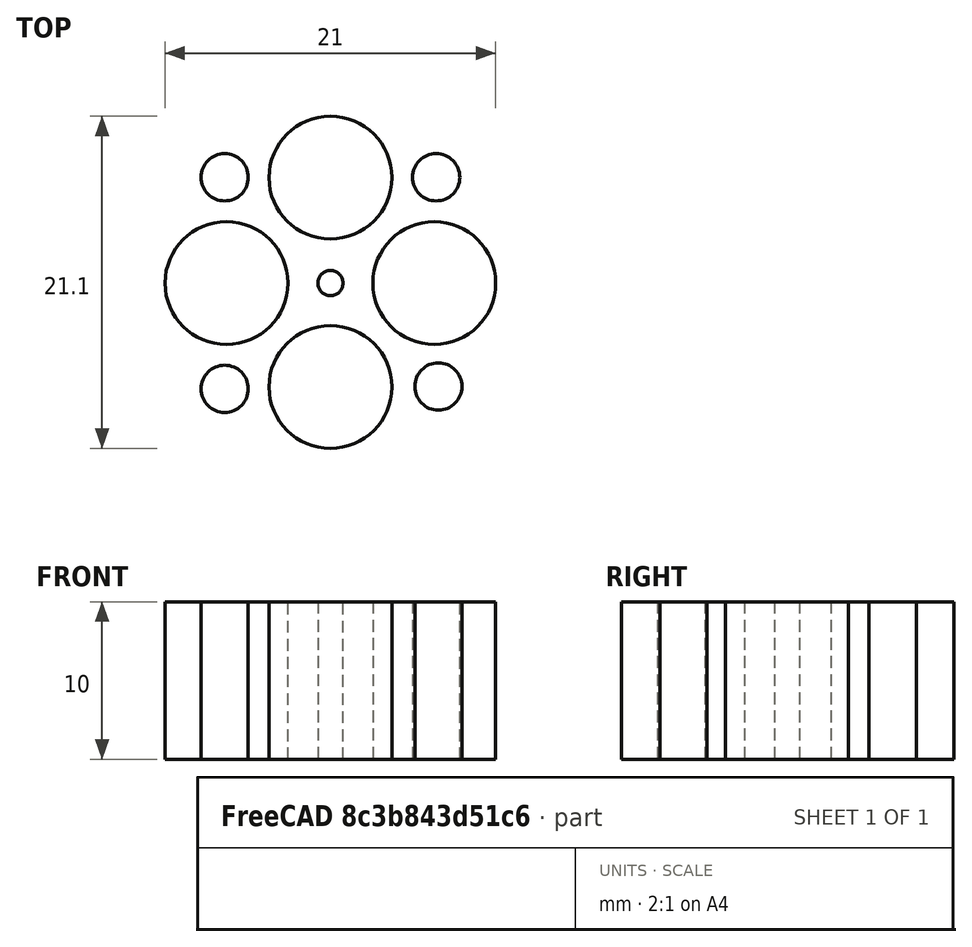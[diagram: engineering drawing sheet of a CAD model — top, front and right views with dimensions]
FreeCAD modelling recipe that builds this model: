
FCSTD DOCUMENT  (FreeCAD 0.19R0.19.2)
Label: 006
License: All rights reserved
LicenseURL: http://en.wikipedia.org/wiki/All_rights_reserved
objects: Sketcher::SketchObject×2, Part::Extrusion×1
note: 3 computed .brp shape members not serialized (recipe doc carries the construction recipe); baked Part::Feature solids carry a one-line shape summary decoded from their .brp

FEATURE [Sketcher::SketchObject] Sketch  label="holes"
  FullyConstrained = true
  sketch-geometry (9):
    g0: Circle CenterX=0 CenterY=0 CenterZ=0 NormalX=0 NormalY=0 NormalZ=1 AngleXU=0 Radius=0.8
    g1: Circle CenterX=0 CenterY=6.7 CenterZ=0 NormalX=0 NormalY=0 NormalZ=1 AngleXU=0 Radius=3.9
    g2: Circle CenterX=6.6 CenterY=0 CenterZ=0 NormalX=0 NormalY=0 NormalZ=1 AngleXU=0 Radius=3.9
    g3: Circle CenterX=-6.6 CenterY=0 CenterZ=0 NormalX=0 NormalY=0 NormalZ=1 AngleXU=0 Radius=3.9
    g4: Circle CenterX=0 CenterY=-6.6 CenterZ=0 NormalX=0 NormalY=0 NormalZ=1 AngleXU=0 Radius=3.9
    g5: Circle CenterX=6.71751 CenterY=6.71751 CenterZ=0 NormalX=0 NormalY=0 NormalZ=1 AngleXU=0 Radius=1.5
    g6: Circle CenterX=-6.71751 CenterY=-6.71751 CenterZ=0 NormalX=0 NormalY=0 NormalZ=1 AngleXU=0 Radius=1.5
    g7: Circle CenterX=-6.71751 CenterY=6.71751 CenterZ=0 NormalX=0 NormalY=0 NormalZ=1 AngleXU=0 Radius=1.5
    g8: Circle CenterX=6.86196 CenterY=-6.56989 CenterZ=0 NormalX=0 NormalY=0 NormalZ=1 AngleXU=0 Radius=1.5
  constraints (9):
    c: Block(g5)
    c: Block(g2)
    c: Block(g1)
    c: Block(g7)
    c: Block(g3)
    c: Block(g6)
    c: Block(g4)
    c: Block(g0)
    c: Block(g8)
FEATURE [Part::Extrusion] Extrude
  Base = -> Sketch
  Dir = (0,0,1)
  DirMode = 2
  FaceMakerClass = Part::FaceMakerBullseye
  LengthFwd = 10
  LengthRev = 0
  Solid = true
  Symmetric = false
FEATURE [Sketcher::SketchObject] Sketch001
  FullyConstrained = false
  Placement = pos=(0,0,0) rot=(0.57735,0.57735,0.57735;2.0944rad)
  sketch-geometry (33):
    g0: Circle CenterX=1.6 CenterY=4 CenterZ=0 NormalX=0 NormalY=0 NormalZ=1 AngleXU=0 Radius=1
    g1: Circle CenterX=1.6 CenterY=2.5 CenterZ=0 NormalX=0 NormalY=0 NormalZ=1 AngleXU=0 Radius=1
    g2: Circle CenterX=3.6 CenterY=2.5 CenterZ=0 NormalX=0 NormalY=0 NormalZ=1 AngleXU=0 Radius=1
    g3: BSplineCurve PolesCount=3 KnotsCount=2 Degree=2 IsPeriodic=0
    g4: GeomPoint X=1.6 Y=4 Z=0
    g5: GeomPoint X=3.6 Y=2.5 Z=0
    g6: Circle CenterX=1.6 CenterY=-4 CenterZ=0 NormalX=0 NormalY=0 NormalZ=1 AngleXU=0 Radius=1
    g7: Circle CenterX=1.6 CenterY=-2.5 CenterZ=0 NormalX=0 NormalY=0 NormalZ=1 AngleXU=0 Radius=1
    g8: Circle CenterX=3.6 CenterY=-2.5 CenterZ=0 NormalX=0 NormalY=0 NormalZ=1 AngleXU=0 Radius=1
    g9: BSplineCurve PolesCount=3 KnotsCount=2 Degree=2 IsPeriodic=0
    g10: GeomPoint X=1.6 Y=-4 Z=0
    g11: GeomPoint X=3.6 Y=-2.5 Z=0
    g12: LineSegment StartX=1.6 StartY=4 StartZ=0 EndX=0 EndY=4 EndZ=0
    g13: Circle CenterX=12.5 CenterY=0.7 CenterZ=0 NormalX=0 NormalY=0 NormalZ=1 AngleXU=0 Radius=1
    g14: Circle CenterX=13.06 CenterY=0 CenterZ=0 NormalX=0 NormalY=0 NormalZ=1 AngleXU=0 Radius=1
    g15: Circle CenterX=12.5 CenterY=-0.7 CenterZ=0 NormalX=0 NormalY=0 NormalZ=1 AngleXU=0 Radius=1
    g16: BSplineCurve PolesCount=3 KnotsCount=2 Degree=2 IsPeriodic=0
    g17: GeomPoint X=12.5 Y=0.7 Z=0
    g18: GeomPoint X=12.5 Y=-0.7 Z=0
    g19: Circle CenterX=3.6 CenterY=2.5 CenterZ=0 NormalX=0 NormalY=0 NormalZ=1 AngleXU=0 Radius=1
    g20: Circle CenterX=3.61896 CenterY=1.5 CenterZ=0 NormalX=0 NormalY=0 NormalZ=1 AngleXU=0 Radius=1
    g21: Circle CenterX=4.81896 CenterY=1.5 CenterZ=0 NormalX=0 NormalY=0 NormalZ=1 AngleXU=0 Radius=1
    g22: BSplineCurve PolesCount=3 KnotsCount=2 Degree=2 IsPeriodic=0
    g23: GeomPoint X=3.6 Y=2.5 Z=0
    g24: GeomPoint X=4.81896 Y=1.5 Z=0
    g25: Circle CenterX=3.6 CenterY=-2.5 CenterZ=0 NormalX=0 NormalY=0 NormalZ=1 AngleXU=0 Radius=1
    g26: Circle CenterX=3.61896 CenterY=-1.5 CenterZ=0 NormalX=0 NormalY=0 NormalZ=1 AngleXU=0 Radius=1
    g27: Circle CenterX=4.81896 CenterY=-1.5 CenterZ=0 NormalX=0 NormalY=0 NormalZ=1 AngleXU=0 Radius=1
    g28: BSplineCurve PolesCount=3 KnotsCount=2 Degree=2 IsPeriodic=0
    g29: GeomPoint X=3.6 Y=-2.5 Z=0
    g30: GeomPoint X=4.81896 Y=-1.5 Z=0
    g31: LineSegment StartX=4.81896 StartY=1.5 StartZ=0 EndX=12.5 EndY=0.7 EndZ=0
    g32: LineSegment StartX=4.81896 StartY=-1.5 StartZ=0 EndX=12.5 EndY=-0.7 EndZ=0
  constraints (50):
    c: Weight(g0) = 1
    c: Equal(g0,g1)
    c: Equal(g0,g2)
    c: InternalAlignment(g0,g3)
    c: InternalAlignment(g1,g3)
    c: InternalAlignment(g2,g3)
    c: InternalAlignment(g4,g3)
    c: InternalAlignment(g5,g3)
    c: Weight(g6) = 1
    c: Equal(g6,g7)
    c: Equal(g6,g8)
    c: InternalAlignment(g6,g9)
    c: InternalAlignment(g7,g9)
    c: InternalAlignment(g8,g9)
    c: InternalAlignment(g10,g9)
    c: InternalAlignment(g11,g9)
    c: Block(g3)
    c: Block(g9)
    c: Coincident(g12,g3)
    c: Horizontal(g12)
    c: Distance(g12) = 1.6
    c: Weight(g13) = 1
    c: Equal(g13,g14)
    c: Equal(g13,g15)
    c: InternalAlignment(g13,g16)
    c: InternalAlignment(g14,g16)
    c: InternalAlignment(g15,g16)
    c: InternalAlignment(g17,g16)
    c: InternalAlignment(g18,g16)
    c: Coincident(g22,g3)
    c: Weight(g19) = 1
    c: Equal(g19,g20)
    c: Equal(g19,g21)
    c: InternalAlignment(g19,g22)
    c: InternalAlignment(g20,g22)
    c: InternalAlignment(g21,g22)
    c: InternalAlignment(g23,g22)
    c: InternalAlignment(g24,g22)
    c: Coincident(g28,g9)
    c: Weight(g25) = 1
    c: Equal(g25,g26)
    c: Equal(g25,g27)
    c: InternalAlignment(g25,g28)
    c: InternalAlignment(g26,g28)
    c: InternalAlignment(g27,g28)
    c: InternalAlignment(g29,g28)
    c: InternalAlignment(g30,g28)
    c: Block(g22)
    c: Block(g28)
    c: Block(g16)
